# Revit family: R1960
name_source: partatom
category: Generic Models
revit_build: Autodesk Revit 2018 (Build: 20170223_1515(x64)
units: mm (PartAtom-declared; Revit-internal decimal feet)

## family parameters
Can host rebar = No
Cut with Voids When Loaded = No
Host = Face
Part Type = Normal
Room Calculation Point = No
Round Connector Dimension = Use Diameter
Shared = No

## types (7) — shared parameters
Default Elevation = 4' - 0"
Description = DOWNSPOUT NOZZLE WITH PERFORATED COVER
Floor Drain Material = Paint - Sherwin Williams Paint - #952C2A - Bellwood Red
Manufacturer = MIFAB
Model = R1960
URL = WWW.MIFAB.COM

## per-type parameters (varying)
| type | A | B | C | Pipe Diameter | Pipe Radius | T |
| R1960_3"_Dia | 0' - 4 1/4" | 0' - 7 3/4" | 0' - 6" | 0' - 3" | 0' - 1 1/2" | 0' - 1 1/4" |
| R1960_4"_Dia | 0' - 5 1/4" | 0' - 8 3/4" | 0' - 7" | 0' - 4" | 0' - 2" | 0' - 1 1/4" |
| R1960_6"_Dia | 0' - 7 1/2" | 0' - 11" | 0' - 9" | 0' - 6" | 0' - 3" | 0' - 1 1/4" |
| R1960_8"_Dia | 0' - 9 1/2" | 1' - 1" | 0' - 11 1/4" | 0' - 8" | 0' - 4" | 0' - 1 1/4" |
| R1960_10"_Dia | 0' - 11 1/2" | 1' - 3" | 1' - 1 1/2" | 0' - 10" | 0' - 5" | 0' - 3" |
| R1960_12"_Dia | 1' - 1 1/2" | 1' - 5" | 1' - 3 1/2" | 1' - 0" | 0' - 6" | 0' - 3" |
| R1960_15"_Dia | 1' - 4 3/4" | 1' - 8" | 1' - 6 1/2" | 1' - 3" | 0' - 7 1/2" | 0' - 4" |

## geometry (parser evidence)
native form markers: Sweep x2
no freeform markers — native parametric forms only
